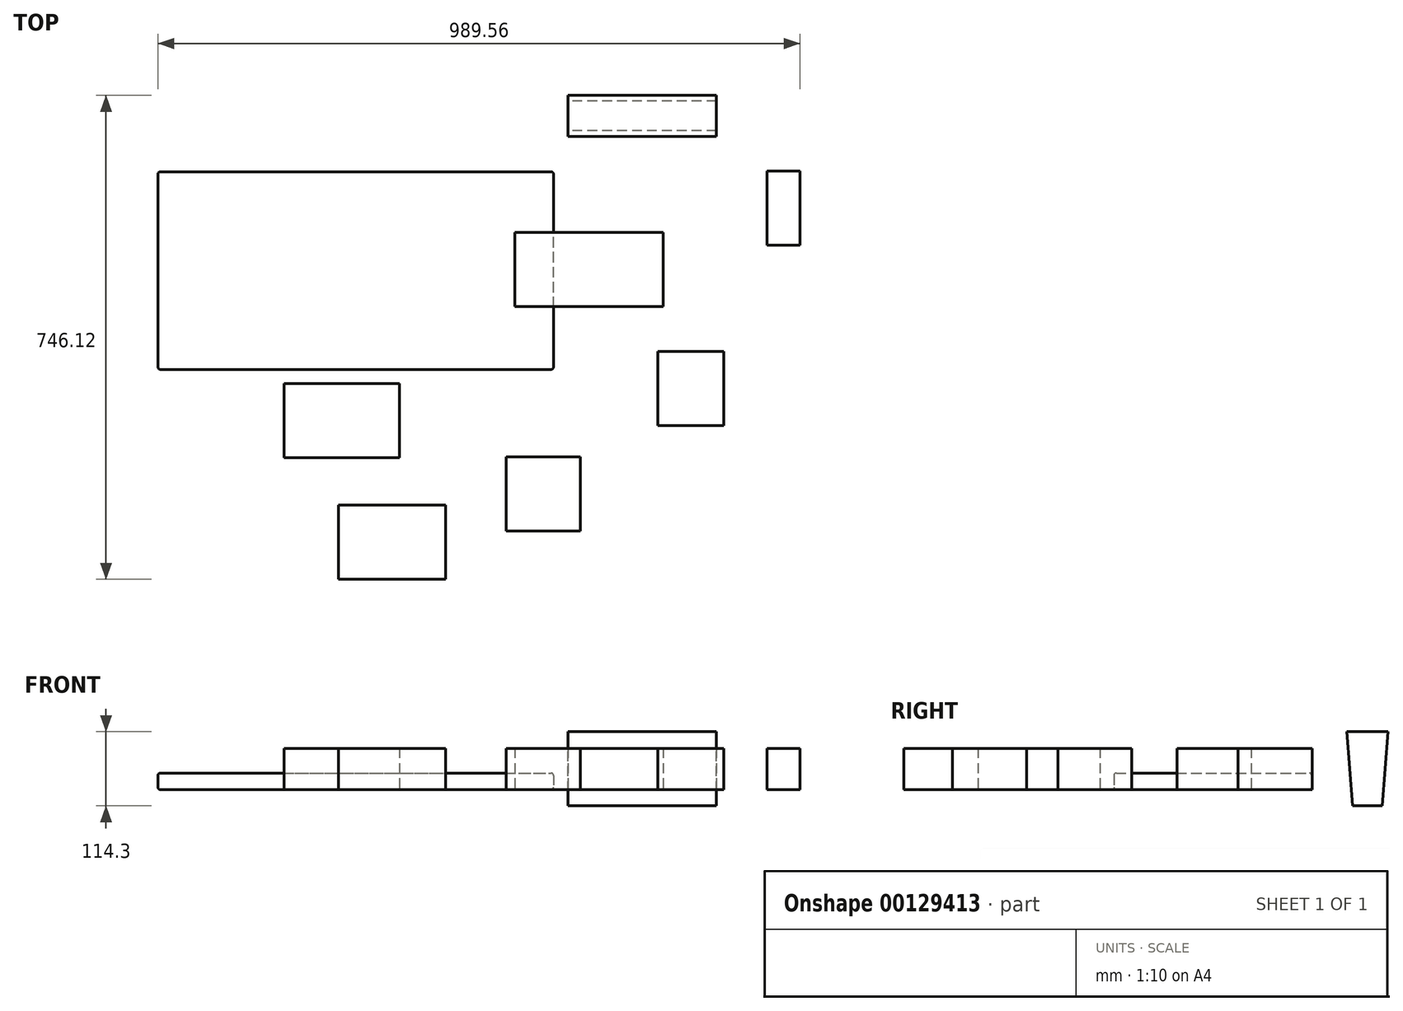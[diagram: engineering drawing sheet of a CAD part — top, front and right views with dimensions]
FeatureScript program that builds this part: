
annotation { "Feature Type Name" : "Feature", "Feature Type Description" : "" }
export const myFeature = defineFeature(function(context is Context, id is Id, definition is map)
    precondition{}
    {
        {
            var Q0;
            Q0=qCreatedBy(makeId("Top.planeOp"),FACE);
            var sketch = newSketch(context, id + "F0", { "sketchPlane" : qUnion([Q0])});
            skLineSegment(sketch, "E0.bottom", {"start": v(-81.86, -44.94) * mm, "end": v(146.74, -44.94) * mm});
            skLineSegment(sketch, "E0.top", {"start": v(-81.86, 69.36) * mm, "end": v(146.74, 69.36) * mm});
            skLineSegment(sketch, "E0.left", {"start": v(-81.86, -44.94) * mm, "end": v(-81.86, 69.36) * mm});
            skLineSegment(sketch, "E0.right", {"start": v(146.74, -44.94) * mm, "end": v(146.74, 69.36) * mm});
            skSolve(sketch);
        }
        {
            var Q0;
            Q0=makeQuery(id+"F0.imprint","IMPRINT",FACE,{"disambiguationData":[TD([[makeQuery(id+"F0.imprint","IMPRINT",EDGE,{"derivedFrom":sQuery(id+"F0.wireOp",EDGE,"E0.bottom")}),1.0]])]});
            extrude(context, id + "F1", {"entities" : qUnion([Q0]), "depth" : 63.5 * mm});
        }
        {
            var Q0;
            Q0=qCreatedBy(makeId("Top.planeOp"),FACE);
            var sketch = newSketch(context, id + "F2", { "sketchPlane" : qUnion([Q0])});
            skLineSegment(sketch, "E1.bottom", {"start": v(-632.15, -142.13) * mm, "end": v(-22.55, -142.13) * mm});
            skLineSegment(sketch, "E1.top", {"start": v(-632.15, 162.67) * mm, "end": v(-22.55, 162.67) * mm});
            skLineSegment(sketch, "E1.left", {"start": v(-632.15, -142.13) * mm, "end": v(-632.15, 162.67) * mm});
            skLineSegment(sketch, "E1.right", {"start": v(-22.55, -142.13) * mm, "end": v(-22.55, 162.67) * mm});
            skSolve(sketch);
        }
        {
            var Q0;
            Q0=makeQuery(id+"F2.imprint","IMPRINT",FACE,{"disambiguationData":[TD([[makeQuery(id+"F2.imprint","IMPRINT",EDGE,{"derivedFrom":sQuery(id+"F2.wireOp",EDGE,"E1.bottom")}),1.0]])]});
            extrude(context, id + "F3", {"entities" : qUnion([Q0]), "depth" : 25.4 * mm});
        }
        {
            var Q0;
            Q0=makeQuery(id+"F3.opExtrude","CAP_EDGE",EDGE,{"disambiguationData":[OSD([sQuery(id+"F2.wireOp",EDGE,"E1.bottom")])],"isStart":false});
            var Q1;
            Q1=makeQuery(id+"F3.opExtrude","CAP_EDGE",EDGE,{"disambiguationData":[OSD([sQuery(id+"F2.wireOp",EDGE,"E1.right")])],"isStart":false});
            var Q2;
            Q2=makeQuery(id+"F3.opExtrude","SWEPT_EDGE",EDGE,{"disambiguationData":[OSD([sQuery(id+"F2.wireOp",EDGE,"E1.bottom"),sQuery(id+"F2.wireOp",EDGE,"E1.right")])]});
            var Q3;
            Q3=makeQuery(id+"F3.opExtrude","CAP_EDGE",EDGE,{"disambiguationData":[OSD([sQuery(id+"F2.wireOp",EDGE,"E1.bottom")])],"isStart":true});
            var Q4;
            Q4=makeQuery(id+"F3.opExtrude","CAP_EDGE",EDGE,{"disambiguationData":[OSD([sQuery(id+"F2.wireOp",EDGE,"E1.right")])],"isStart":true});
            var Q5;
            Q5=makeQuery(id+"F3.opExtrude","SWEPT_EDGE",EDGE,{"disambiguationData":[OSD([sQuery(id+"F2.wireOp",EDGE,"E1.bottom"),sQuery(id+"F2.wireOp",EDGE,"E1.left")])]});
            var Q6;
            Q6=makeQuery(id+"F3.opExtrude","CAP_EDGE",EDGE,{"disambiguationData":[OSD([sQuery(id+"F2.wireOp",EDGE,"E1.left")])],"isStart":false});
            var Q7;
            Q7=makeQuery(id+"F3.opExtrude","CAP_EDGE",EDGE,{"disambiguationData":[OSD([sQuery(id+"F2.wireOp",EDGE,"E1.left")])],"isStart":true});
            var Q8;
            Q8=makeQuery(id+"F3.opExtrude","SWEPT_EDGE",EDGE,{"disambiguationData":[OSD([sQuery(id+"F2.wireOp",EDGE,"E1.top"),sQuery(id+"F2.wireOp",EDGE,"E1.left")])]});
            var Q9;
            Q9=makeQuery(id+"F3.opExtrude","CAP_EDGE",EDGE,{"disambiguationData":[OSD([sQuery(id+"F2.wireOp",EDGE,"E1.top")])],"isStart":false});
            var Q10;
            Q10=makeQuery(id+"F3.opExtrude","CAP_EDGE",EDGE,{"disambiguationData":[OSD([sQuery(id+"F2.wireOp",EDGE,"E1.top")])],"isStart":true});
            var Q11;
            Q11=makeQuery(id+"F3.opExtrude","SWEPT_EDGE",EDGE,{"disambiguationData":[OSD([sQuery(id+"F2.wireOp",EDGE,"E1.top"),sQuery(id+"F2.wireOp",EDGE,"E1.right")])]});
            fillet(context, id + "F4", {"entities" : qUnion([Q0, Q1, Q2, Q3, Q4, Q5, Q6, Q7, Q8, Q9, Q10, Q11]), "radius" : 3.8 * mm, "tangentPropagation" : true, "allowEdgeOverflow" : false});
        }
        {
            var Q0;
            Q0=qCreatedBy(makeId("Top.planeOp"),FACE);
            var sketch = newSketch(context, id + "F5", { "sketchPlane" : qUnion([Q0])});
            skLineSegment(sketch, "E2.bottom", {"start": v(138.22, -114.33) * mm, "end": v(239.82, -114.33) * mm});
            skLineSegment(sketch, "E2.top", {"start": v(138.22, -228.63) * mm, "end": v(239.82, -228.63) * mm});
            skLineSegment(sketch, "E2.left", {"start": v(138.22, -114.33) * mm, "end": v(138.22, -228.63) * mm});
            skLineSegment(sketch, "E2.right", {"start": v(239.82, -114.33) * mm, "end": v(239.82, -228.63) * mm});
            skSolve(sketch);
        }
        {
            var Q0;
            Q0=makeQuery(id+"F5.imprint","IMPRINT",FACE,{"disambiguationData":[TD([[makeQuery(id+"F5.imprint","IMPRINT",EDGE,{"derivedFrom":sQuery(id+"F5.wireOp",EDGE,"E2.bottom")}),-1.0]])]});
            extrude(context, id + "F6", {"entities" : qUnion([Q0]), "depth" : 63.5 * mm});
        }
        {
            var Q0;
            Q0=qCreatedBy(makeId("Top.planeOp"),FACE);
            var sketch = newSketch(context, id + "F7", { "sketchPlane" : qUnion([Q0])});
            skLineSegment(sketch, "E3.bottom", {"start": v(-437.44, -163.78) * mm, "end": v(-259.64, -163.78) * mm});
            skLineSegment(sketch, "E3.top", {"start": v(-437.44, -278.08) * mm, "end": v(-259.64, -278.08) * mm});
            skLineSegment(sketch, "E3.left", {"start": v(-437.44, -163.78) * mm, "end": v(-437.44, -278.08) * mm});
            skLineSegment(sketch, "E3.right", {"start": v(-259.64, -163.78) * mm, "end": v(-259.64, -278.08) * mm});
            skSolve(sketch);
        }
        {
            var Q0;
            Q0=makeQuery(id+"F7.imprint","IMPRINT",FACE,{"disambiguationData":[TD([[makeQuery(id+"F7.imprint","IMPRINT",EDGE,{"derivedFrom":sQuery(id+"F7.wireOp",EDGE,"E3.bottom")}),-1.0]])]});
            extrude(context, id + "F8", {"entities" : qUnion([Q0]), "depth" : 63.5 * mm});
        }
        {
            var Q0;
            Q0=qCreatedBy(makeId("Top.planeOp"),FACE);
            var sketch = newSketch(context, id + "F9", { "sketchPlane" : qUnion([Q0])});
            skLineSegment(sketch, "E4.bottom", {"start": v(-95.52, -276.64) * mm, "end": v(18.78, -276.64) * mm});
            skLineSegment(sketch, "E4.top", {"start": v(-95.52, -390.94) * mm, "end": v(18.78, -390.94) * mm});
            skLineSegment(sketch, "E4.left", {"start": v(-95.52, -276.64) * mm, "end": v(-95.52, -390.94) * mm});
            skLineSegment(sketch, "E4.right", {"start": v(18.78, -276.64) * mm, "end": v(18.78, -390.94) * mm});
            skSolve(sketch);
        }
        {
            var Q0;
            Q0=makeQuery(id+"F9.imprint","IMPRINT",FACE,{"disambiguationData":[TD([[makeQuery(id+"F9.imprint","IMPRINT",EDGE,{"derivedFrom":sQuery(id+"F9.wireOp",EDGE,"E4.bottom")}),-1.0]])]});
            extrude(context, id + "F10", {"entities" : qUnion([Q0]), "depth" : 63.5 * mm});
        }
        {
            var Q0;
            Q0=qCreatedBy(makeId("Top.planeOp"),FACE);
            var sketch = newSketch(context, id + "F11", { "sketchPlane" : qUnion([Q0])});
            skLineSegment(sketch, "E5.bottom", {"start": v(-188.97, -465.71) * mm, "end": v(-354.07, -465.71) * mm});
            skLineSegment(sketch, "E5.top", {"start": v(-188.97, -351.41) * mm, "end": v(-354.07, -351.41) * mm});
            skLineSegment(sketch, "E5.left", {"start": v(-188.97, -465.71) * mm, "end": v(-188.97, -351.41) * mm});
            skLineSegment(sketch, "E5.right", {"start": v(-354.07, -465.71) * mm, "end": v(-354.07, -351.41) * mm});
            skSolve(sketch);
        }
        {
            var Q0;
            Q0=makeQuery(id+"F11.imprint","IMPRINT",FACE,{"disambiguationData":[TD([[makeQuery(id+"F11.imprint","IMPRINT",EDGE,{"derivedFrom":sQuery(id+"F11.wireOp",EDGE,"E5.bottom")}),-1.0]])]});
            extrude(context, id + "F12", {"entities" : qUnion([Q0]), "depth" : 63.5 * mm});
        }
        {
            var Q0;
            Q0=qCreatedBy(makeId("Top.planeOp"),FACE);
            var sketch = newSketch(context, id + "F13", { "sketchPlane" : qUnion([Q0])});
            skLineSegment(sketch, "E6.bottom", {"start": v(306.61, 163.8) * mm, "end": v(357.41, 163.8) * mm});
            skLineSegment(sketch, "E6.top", {"start": v(306.61, 49.5) * mm, "end": v(357.41, 49.5) * mm});
            skLineSegment(sketch, "E6.left", {"start": v(306.61, 163.8) * mm, "end": v(306.61, 49.5) * mm});
            skLineSegment(sketch, "E6.right", {"start": v(357.41, 163.8) * mm, "end": v(357.41, 49.5) * mm});
            skSolve(sketch);
        }
        {
            var Q0;
            Q0=makeQuery(id+"F13.imprint","IMPRINT",FACE,{"disambiguationData":[TD([[makeQuery(id+"F13.imprint","IMPRINT",EDGE,{"derivedFrom":sQuery(id+"F13.wireOp",EDGE,"E6.bottom")}),-1.0]])]});
            extrude(context, id + "F14", {"entities" : qUnion([Q0]), "depth" : 63.5 * mm});
        }
        {
            var Q0;
            Q0=qCreatedBy(makeId("Right.planeOp"),FACE);
            var sketch = newSketch(context, id + "F15", { "sketchPlane" : qUnion([Q0])});
            skLineSegment(sketch, "E7.bottom", {"start": v(216.9, 89.16) * mm, "end": v(280.4, 89.16) * mm});
            skLineSegment(sketch, "E7.top", {"start": v(216.9, -25.14) * mm, "end": v(280.4, -25.14) * mm});
            skLineSegment(sketch, "E7.left", {"start": v(216.9, 89.16) * mm, "end": v(216.9, -25.14) * mm});
            skLineSegment(sketch, "E7.right", {"start": v(280.4, 89.16) * mm, "end": v(280.4, -25.14) * mm});
            skPoint(sketch, "E8", {"position": v(248.66, -25.14) * mm});
            skPoint(sketch, "E9", {"position": v(225.8, -25.14) * mm});
            skPoint(sketch, "E10", {"position": v(271.52, -25.14) * mm});
            skLineSegment(sketch, "E11", {"start": v(216.9, 89.16) * mm, "end": v(225.8, -25.14) * mm});
            skLineSegment(sketch, "E12", {"start": v(271.52, -25.14) * mm, "end": v(280.4, 89.16) * mm});
            skSolve(sketch);
        }
        {
            var Q0;
            Q0=makeQuery(id+"F15.imprint","IMPRINT",FACE,{"disambiguationData":[TD([[makeQuery(id+"F15.imprint","IMPRINT",EDGE,{"derivedFrom":sQuery(id+"F15.wireOp",EDGE,"E7.bottom")}),-1.0]])]});
            extrude(context, id + "F16", {"entities" : qUnion([Q0]), "depth" : 228.6 * mm});
        }
    });
